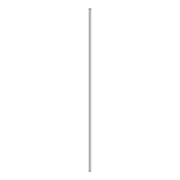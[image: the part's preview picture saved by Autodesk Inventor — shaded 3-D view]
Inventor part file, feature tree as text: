
AUTODESK INVENTOR PART (.ipt)
format: ipt  version: 2022 (Build 260153000, 153)  size: 75,264 bytes
history: native  units: mm
features: other x1, extrude x1, sketch x1
ambient origin geometry x8: Origin, YZ Plane, XZ Plane, XY Plane, X Axis, Y Axis, Z Axis, Center Point
bodies: Body1 (feature_tree)
feature tree (3):
  other  "Твердое тело1"
  extrude  "Выдавливание1"  Depth=8.0mm
  sketch  "Эскиз1"
